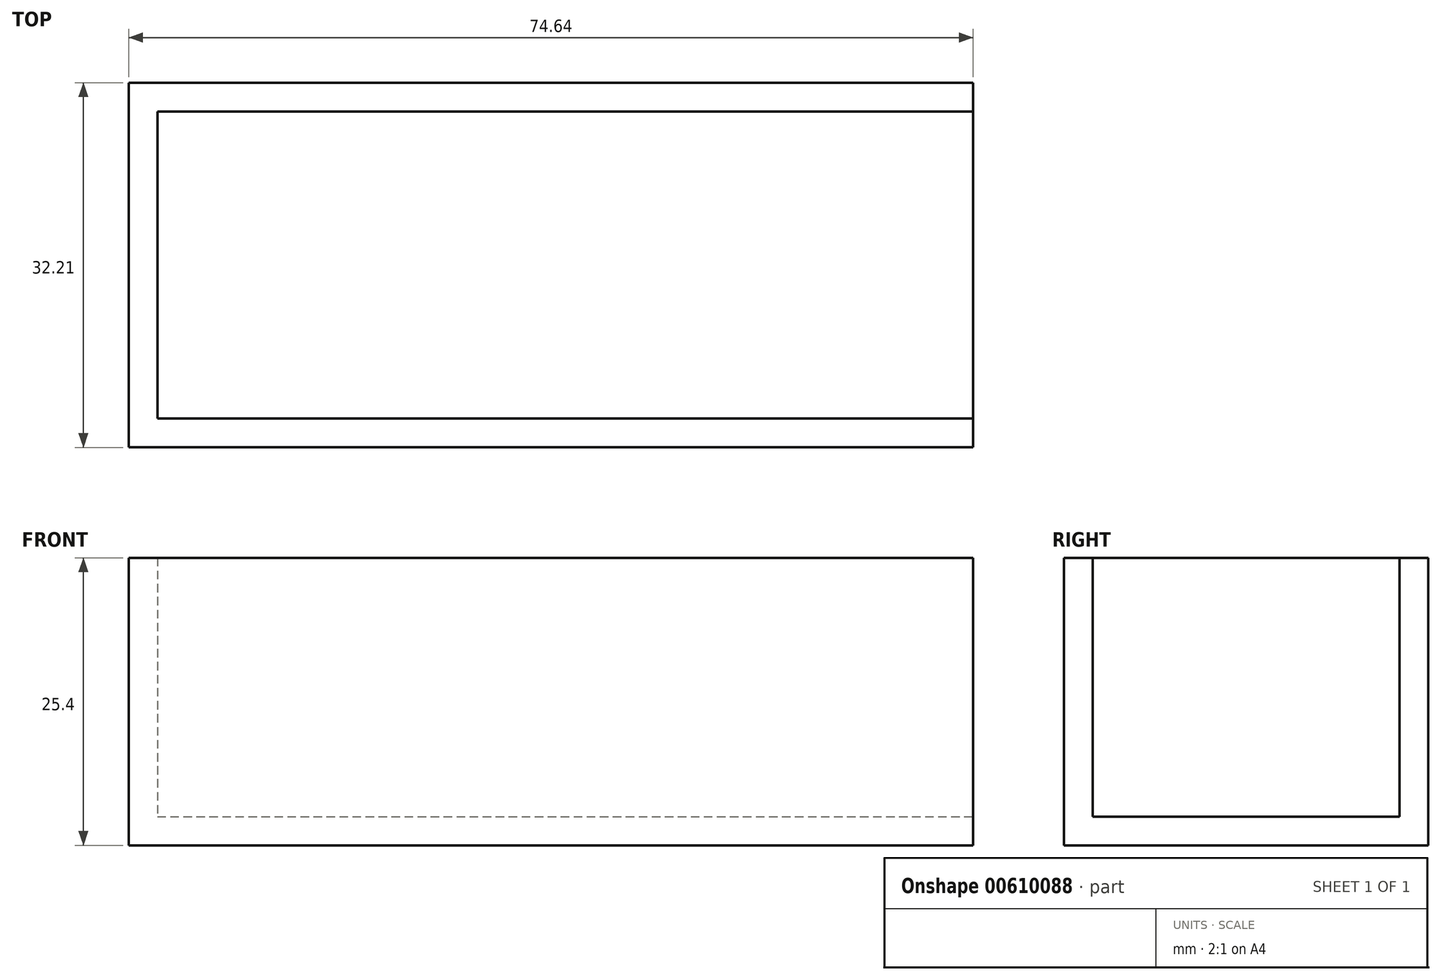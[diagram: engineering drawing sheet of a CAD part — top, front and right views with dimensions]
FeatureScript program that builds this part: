
annotation { "Feature Type Name" : "Feature", "Feature Type Description" : "" }
export const myFeature = defineFeature(function(context is Context, id is Id, definition is map)
    precondition{}
    {
        {
            var Q0;
            Q0=qCreatedBy(makeId("Top.planeOp"),FACE);
            var sketch = newSketch(context, id + "F0", { "sketchPlane" : qUnion([Q0])});
            skLineSegment(sketch, "E0", {"start": v(-88.06, 22.11) * mm, "end": v(-13.42, 22.11) * mm});
            skLineSegment(sketch, "E1", {"start": v(-13.42, 22.11) * mm, "end": v(-13.42, -10.1) * mm});
            skLineSegment(sketch, "E2", {"start": v(-88.06, 22.11) * mm, "end": v(-88.06, -10.1) * mm});
            skLineSegment(sketch, "E3", {"start": v(-88.06, -10.1) * mm, "end": v(-13.42, -10.1) * mm});
            skPoint(sketch, "E4", {"position": v(-34.85, 8.59) * mm});
            skSolve(sketch);
        }
        {
            var Q0;
            Q0 = qSketchRegion(id + "F0", true);
            extrude(context, id + "F1", {"entities" : qUnion([Q0]), "depth" : 25.4 * mm, "offsetDistance" : 25.4 * mm});
        }
        {
            var Q0;
            Q0=makeQuery(id+"F1.opExtrude","CAP_FACE",FACE,{"disambiguationData":[OSD([sQuery(id+"F0.wireOp",EDGE,"E0"),sQuery(id+"F0.wireOp",EDGE,"E1"),sQuery(id+"F0.wireOp",EDGE,"E2"),sQuery(id+"F0.wireOp",EDGE,"E3")])],"isStart":false});
            var Q1;
            Q1=makeQuery(id+"F1.opExtrude","SWEPT_FACE",FACE,{"disambiguationData":[OSD([sQuery(id+"F0.wireOp",EDGE,"E1")])]});
            shell(context, id + "F2", {"entities" : qUnion([Q0, Q1]), "thickness" : 2.54 * mm});
        }
    });
